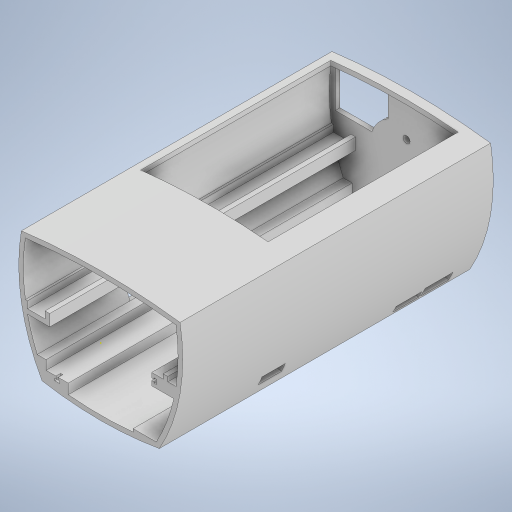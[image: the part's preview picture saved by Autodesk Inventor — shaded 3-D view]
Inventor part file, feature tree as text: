
AUTODESK INVENTOR PART (.ipt)
format: ipt  version: 2023 (Build 270158000, 158)  size: 482,816 bytes
history: native  units: in
note: dims shown in document units (in); Inventor stores cm internally (conversion verified against a paired STEP export)
features: extrude x10, sketch x9, plane x4, projected_geometry x1
ambient origin geometry x8: Origin, YZ Plane, XZ Plane, XY Plane, X Axis, Y Axis, Z Axis, Center Point
bodies: Body1 (feature_tree)
feature tree (24):
  sketch  "Sketch1"  dims[d19=2.5591in d20=0.9055in]
  extrude  "Extrusion3"  Depth=0.9055in
  extrude  "Extrusion4"  Depth=1.8898in
  plane  "Work Plane2"
  sketch  "Sketch2"  dims[d30=2.5591in d39=1.8898in]
  extrude  "Extrusion5"  Depth=0.9843in
  sketch  "Sketch3"  dims[d40=0.9843in d41=0.3346in]
  plane  "Work Plane4"
  extrude  "Extrusion7"  Depth=0.0787in
  extrude  "Extrusion8"  Depth=0.0787in
  extrude  "Extrusion9"  Depth=0.1969in
  plane  "Work Plane5"
  extrude  "Extrusion10"  Depth=0.3937in
  plane  "Work Plane6"
  extrude  "Extrusion11"  Depth=0.0787in
  extrude  "Extrusion12"  Depth=3.937in TaperAngle=0.0deg
  sketch  "Sketch9"  dims[d54=0.1181in d55=0.0787in]
  extrude  "Extrusion13"  Depth=0.0787in TaperAngle=0.0deg
  projected_geometry  "Projected Loop1"
  sketch  "Sketch5"  dims[d42=0.3346in d43=0.0787in]
  sketch  "Sketch6"  dims[d44=0.0787in d45=2.126in]
  sketch  "Sketch7"  dims[d46=0.1969in d47=0.1969in]
  sketch  "Sketch8"  dims[d48=0.3937in d49=0.3937in]
  sketch  "Sketch10"  dims[d56=0.0787in d57=3.937in d58=0.0in d59=0.0787in d60=0.0in d61=0.2756in d62=2.2835in d63=0.1364in d64=3.2283in d65=90.0deg d66=0.0787in d67=0.0in d68=0.1181in d69=0.0787in d70=0.0787in d73=0.0787in d74=0.3937in d76=0.315in d77=0.1575in d78=0.4724in d79=0.0394in d80=0.1181in d81=0.4331in d82=0.3937in d83=0.0in d84=0.0787in d85=0.1575in d86=0.3937in d87=0.0in d88=0.0787in d89=0.3937in d90=0.0in d91=3.2283in d92=0.315in d93=0.3937in d94=0.1575in d95=3.2283in d96=0.1575in d97=0.3937in d98=0.3937in d99=0.0in d100=1.2598in d101=0.0in d102=1.2598in d104=0.1181in d106=0.1181in d107=1.2598in d108=0.0in d110=0.0394in d111=0.0394in d112=0.0394in d113=0.0787in d116=0.0394in d117=0.0787in d118=0.0394in d119=0.0787in d120=0.0in d121=0.3937in d122=0.3937in d123=0.9055in d124=0.9843in d125=1.2795in d126=0.0787in d127=0.0787in d128=0.313in d129=0.5467in d130=0.8983in d131=0.6979in d103=0.0344in]
